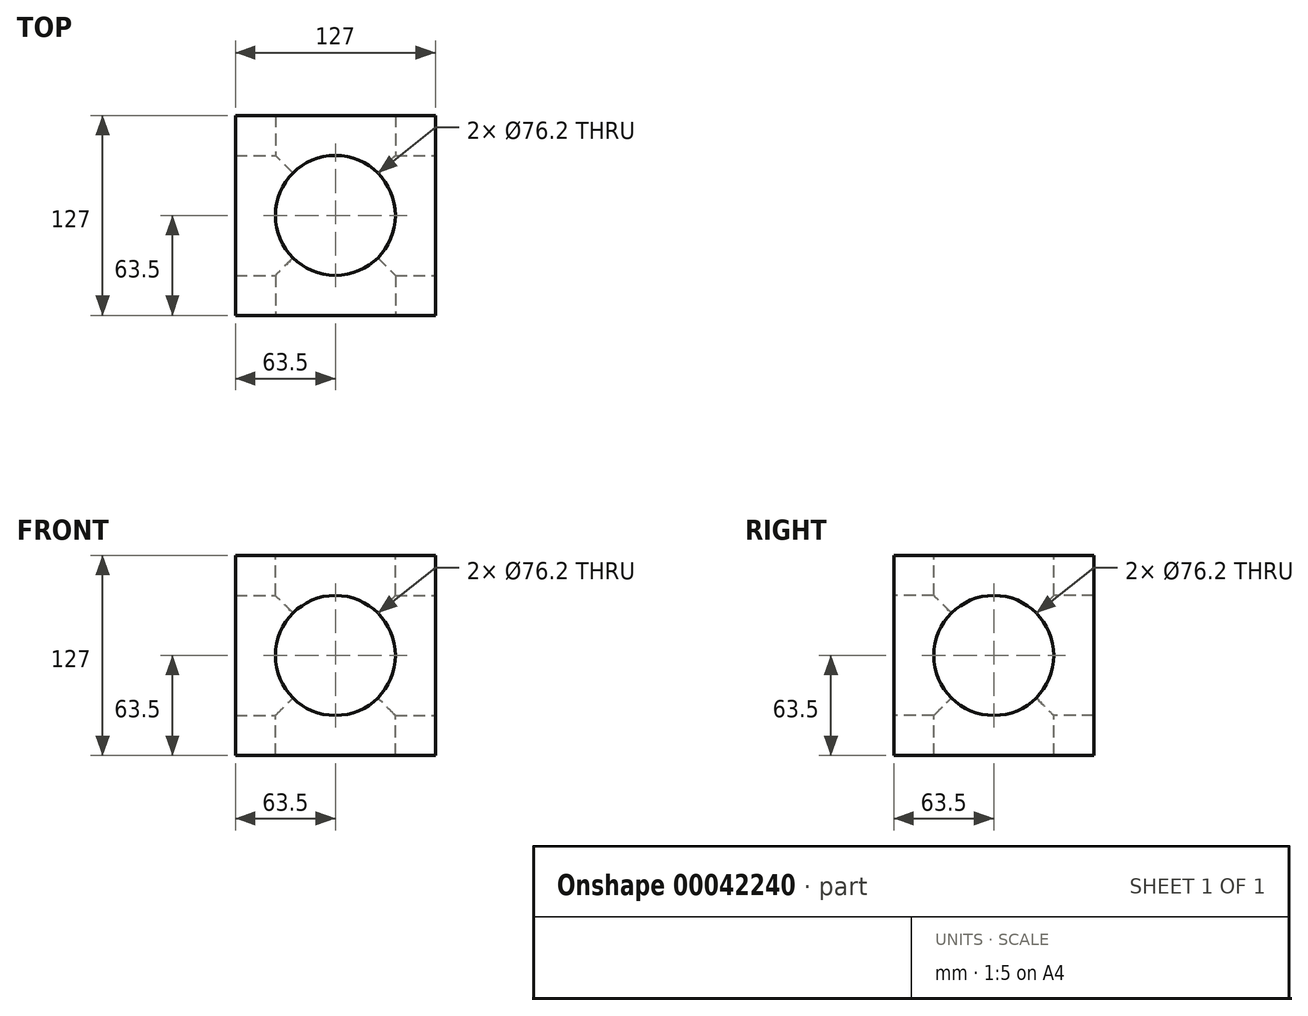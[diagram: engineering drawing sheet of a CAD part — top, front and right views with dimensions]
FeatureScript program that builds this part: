
annotation { "Feature Type Name" : "Feature", "Feature Type Description" : "" }
export const myFeature = defineFeature(function(context is Context, id is Id, definition is map)
    precondition{}
    {
        {
            var Q0;
            Q0=qCreatedBy(makeId("Front.planeOp"),FACE);
            var sketch = newSketch(context, id + "F0", { "sketchPlane" : qUnion([Q0])});
            skLineSegment(sketch, "E0", {"start": v(0, 0) * mm, "end": v(127, 0) * mm});
            skLineSegment(sketch, "E1", {"start": v(127, 0) * mm, "end": v(127, 127) * mm});
            skLineSegment(sketch, "E2", {"start": v(127, 127) * mm, "end": v(0, 127) * mm});
            skLineSegment(sketch, "E3", {"start": v(0, 127) * mm, "end": v(0, 0) * mm});
            skSolve(sketch);
        }
        {
            var Q0;
            Q0=makeQuery(id+"F0.imprint","IMPRINT",FACE,{"disambiguationData":[TD([[makeQuery(id+"F0.imprint","IMPRINT",EDGE,{"derivedFrom":sQuery(id+"F0.wireOp",EDGE,"E0")}),1.0]])]});
            extrude(context, id + "F1", {"entities" : qUnion([Q0]), "depth" : 127 * mm});
        }
        {
            var Q0;
            Q0=makeQuery(id+"F1.opExtrude","SWEPT_FACE",FACE,{"disambiguationData":[OSD([sQuery(id+"F0.wireOp",EDGE,"E1")])]});
            var sketch = newSketch(context, id + "F2", { "sketchPlane" : qUnion([Q0])});
            skCircle(sketch, "E4", {"center": v(-63.5, 63.5) * mm, "radius": 38.1 * mm});
            skSolve(sketch);
        }
        {
            var Q0;
            Q0 = qSketchRegion(id + "F2", true);
            extrude(context, id + "F3", {"entities" : qUnion([Q0]), "operationType" : NewBodyOperationType.REMOVE, "oppositeDirection" : true, "depth" : 127 * mm});
        }
        {
            var Q0;
            Q0=makeQuery(id+"F1.opExtrude","CAP_FACE",FACE,{"disambiguationData":[OSD([sQuery(id+"F0.wireOp",EDGE,"E0"),sQuery(id+"F0.wireOp",EDGE,"E1"),sQuery(id+"F0.wireOp",EDGE,"E2"),sQuery(id+"F0.wireOp",EDGE,"E3")])],"isStart":false});
            var sketch = newSketch(context, id + "F4", { "sketchPlane" : qUnion([Q0])});
            skCircle(sketch, "E5", {"center": v(63.5, 63.5) * mm, "radius": 38.1 * mm});
            skSolve(sketch);
        }
        {
            var Q0;
            Q0 = qSketchRegion(id + "F4", true);
            extrude(context, id + "F5", {"entities" : qUnion([Q0]), "operationType" : NewBodyOperationType.REMOVE, "oppositeDirection" : true, "depth" : 127 * mm});
        }
        {
            var Q0;
            Q0=makeQuery(id+"F1.opExtrude","SWEPT_FACE",FACE,{"disambiguationData":[OSD([sQuery(id+"F0.wireOp",EDGE,"E2")])]});
            var sketch = newSketch(context, id + "F6", { "sketchPlane" : qUnion([Q0])});
            skCircle(sketch, "E6", {"center": v(63.5, -63.5) * mm, "radius": 38.1 * mm});
            skSolve(sketch);
        }
        {
            var Q0;
            Q0=makeQuery(id+"F6.imprint","IMPRINT",FACE,{"disambiguationData":[TD([[makeQuery(id+"F6.imprint","IMPRINT",EDGE,{"derivedFrom":sQuery(id+"F6.wireOp",EDGE,"E6")}),1.0]])]});
            extrude(context, id + "F7", {"entities" : qUnion([Q0]), "operationType" : NewBodyOperationType.REMOVE, "oppositeDirection" : true, "depth" : 127 * mm});
        }
    });
